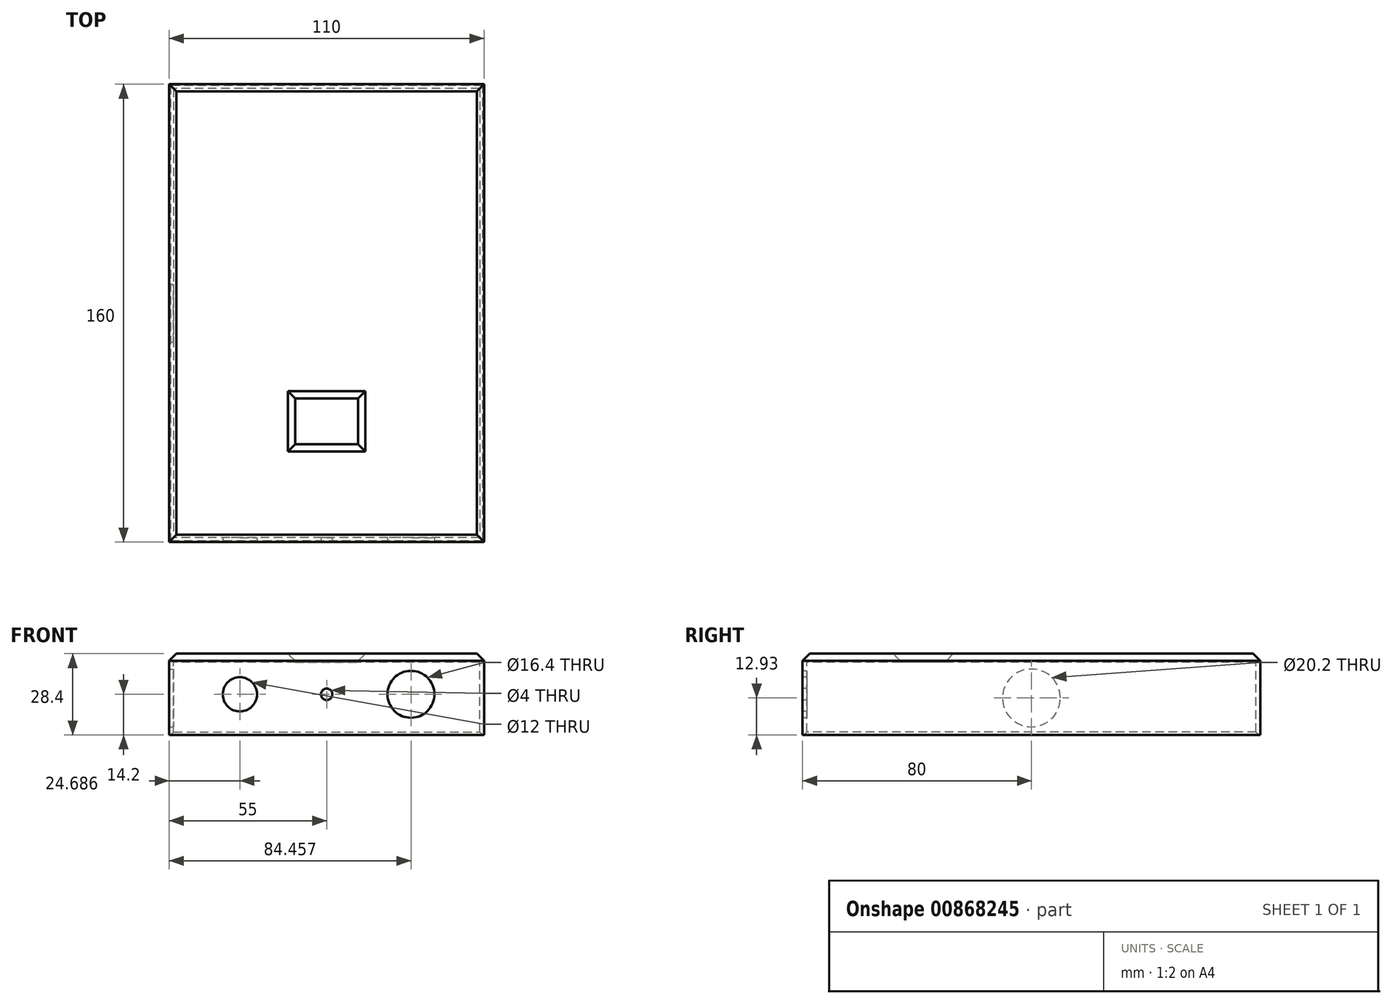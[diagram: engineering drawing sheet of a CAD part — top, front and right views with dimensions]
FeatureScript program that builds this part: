
annotation { "Feature Type Name" : "Feature", "Feature Type Description" : "" }
export const myFeature = defineFeature(function(context is Context, id is Id, definition is map)
    precondition{}
    {
        {
            var Q0;
            Q0=qCreatedBy(makeId("Top.planeOp"),FACE);
            var sketch = newSketch(context, id + "F0", { "sketchPlane" : qUnion([Q0])});
            skLineSegment(sketch, "E0.bottom", {"start": v(-55, -80) * mm, "end": v(55, -80) * mm});
            skLineSegment(sketch, "E0.top", {"start": v(-55, 80) * mm, "end": v(55, 80) * mm});
            skLineSegment(sketch, "E0.left", {"start": v(-55, -80) * mm, "end": v(-55, 80) * mm});
            skLineSegment(sketch, "E0.right", {"start": v(55, -80) * mm, "end": v(55, 80) * mm});
            skPoint(sketch, "E0.middle", {"position": v(0, 0) * mm});
            skLineSegment(sketch, "E1.bottom", {"start": v(-11, -29.82) * mm, "end": v(11, -29.82) * mm});
            skLineSegment(sketch, "E1.top", {"start": v(-11, -45.82) * mm, "end": v(11, -45.82) * mm});
            skLineSegment(sketch, "E1.left", {"start": v(-11, -29.82) * mm, "end": v(-11, -45.82) * mm});
            skLineSegment(sketch, "E1.right", {"start": v(11, -29.82) * mm, "end": v(11, -45.82) * mm});
            skPoint(sketch, "E1.middle", {"position": v(0, -37.82) * mm});
            skSolve(sketch);
        }
        {
            var Q0;
            Q0=makeQuery(id+"F0.imprint","IMPRINT",FACE,{"disambiguationData":[TD([[makeQuery(id+"F0.imprint","IMPRINT",EDGE,{"derivedFrom":sQuery(id+"F0.wireOp",EDGE,"E0.bottom")}),1.0]])]});
            extrude(context, id + "F1", {"entities" : qUnion([Q0]), "depth" : 3 * mm, "offsetDistance" : 25.4 * mm});
        }
        {
            var Q0;
            Q0=makeQuery(id+"F1.opExtrude","CAP_FACE",FACE,{"disambiguationData":[OSD([sQuery(id+"F0.wireOp",EDGE,"E0.bottom"),sQuery(id+"F0.wireOp",EDGE,"E0.top"),sQuery(id+"F0.wireOp",EDGE,"E0.left"),sQuery(id+"F0.wireOp",EDGE,"E0.right")])],"isStart":true});
            var sketch = newSketch(context, id + "F2", { "sketchPlane" : qUnion([Q0])});
            skLineSegment(sketch, "E2.bottom", {"start": v(53.5, -78.5) * mm, "end": v(-53.5, -78.5) * mm});
            skLineSegment(sketch, "E2.top", {"start": v(53.5, 78.5) * mm, "end": v(-53.5, 78.5) * mm});
            skLineSegment(sketch, "E2.left", {"start": v(53.5, -78.5) * mm, "end": v(53.5, 78.5) * mm});
            skLineSegment(sketch, "E2.right", {"start": v(-53.5, -78.5) * mm, "end": v(-53.5, 78.5) * mm});
            skPoint(sketch, "E2.middle", {"position": v(0, 0) * mm});
            skSolve(sketch);
        }
        {
            var Q0;
            Q0=makeQuery(id+"F2.imprint","IMPRINT",FACE,{"disambiguationData":[TD([[makeQuery(id+"F2.imprint","IMPRINT",EDGE,{"derivedFrom":sQuery(id+"F2.wireOp",EDGE,"E2.bottom")}),1.0]])]});
            extrude(context, id + "F3", {"entities" : qUnion([Q0]), "operationType" : NewBodyOperationType.ADD, "depth" : 25.4 * mm, "offsetDistance" : 25.4 * mm});
        }
        {
            var Q0;
            {var subQ0=sQuery(id+"F0.wireOp",EDGE,"E0.bottom");Q0=makeQuery(id+"F3.boolean.opBoolean","MERGE",FACE,{"derivedFrom":[makeQuery(id+"F1.opExtrude","SWEPT_FACE",FACE,{"disambiguationData":[OSD([subQ0])]}),makeQuery(id+"F3.opExtrude","SWEPT_FACE",FACE,{"disambiguationData":[OSD([subQ0])]})]});}
            var sketch = newSketch(context, id + "F4", { "sketchPlane" : qUnion([Q0])});
            skCircle(sketch, "E3", {"center": v(0, -11.2) * mm, "radius": 2 * mm});
            skPoint(sketch, "E3.centerSnap0", {"position": v(55, -11.2) * mm});
            skCircle(sketch, "E4", {"center": v(29.46, -11.2) * mm, "radius": 8.2 * mm});
            skCircle(sketch, "E5", {"center": v(-30.31, -11.2) * mm, "radius": 6 * mm});
            skPoint(sketch, "E5.centerSnap0", {"position": v(-55, -11.2) * mm});
            skSolve(sketch);
        }
        {
            var Q0;
            Q0=sQuery(id+"F4.wireOp",VERTEX,"E4.center");
            var Q1;
            Q1=makeQuery(id+"F1.opExtrude","SWEPT_BODY",BODY,{"disambiguationData":[OSD([sQuery(id+"F0.wireOp",EDGE,"E0.bottom"),sQuery(id+"F0.wireOp",EDGE,"E0.top"),sQuery(id+"F0.wireOp",EDGE,"E0.left"),sQuery(id+"F0.wireOp",EDGE,"E0.right")])]});
            hole(context, id + "F5", {"style" : HoleStyle.SIMPLE, "endStyle" : HoleEndStyle.BLIND, "holeDiameter" : 16.4 * mm, "majorDiameter" : 6.35 * mm, "holeDepth" : 7.62 * mm, "isTappedThrough" : true, "tappedDepth" : 12.7 * mm, "tapClearance" : 3, "locations" : qUnion([Q0]), "scope" : qUnion([Q1])});
        }
        {
            var Q0;
            Q0=sQuery(id+"F4.wireOp",VERTEX,"E3.center");
            var Q1;
            Q1=makeQuery(id+"F1.opExtrude","SWEPT_BODY",BODY,{"disambiguationData":[OSD([sQuery(id+"F0.wireOp",EDGE,"E0.bottom"),sQuery(id+"F0.wireOp",EDGE,"E0.top"),sQuery(id+"F0.wireOp",EDGE,"E0.left"),sQuery(id+"F0.wireOp",EDGE,"E0.right")])]});
            hole(context, id + "F6", {"style" : HoleStyle.SIMPLE, "endStyle" : HoleEndStyle.BLIND, "holeDiameter" : 4 * mm, "majorDiameter" : 6.35 * mm, "holeDepth" : 7.62 * mm, "isTappedThrough" : true, "tappedDepth" : 12.7 * mm, "tapClearance" : 3, "locations" : qUnion([Q0]), "scope" : qUnion([Q1])});
        }
        {
            var Q0;
            Q0=sQuery(id+"F4.wireOp",VERTEX,"E5.center");
            var Q1;
            Q1=makeQuery(id+"F1.opExtrude","SWEPT_BODY",BODY,{"disambiguationData":[OSD([sQuery(id+"F0.wireOp",EDGE,"E0.bottom"),sQuery(id+"F0.wireOp",EDGE,"E0.top"),sQuery(id+"F0.wireOp",EDGE,"E0.left"),sQuery(id+"F0.wireOp",EDGE,"E0.right")])]});
            hole(context, id + "F7", {"style" : HoleStyle.SIMPLE, "endStyle" : HoleEndStyle.BLIND, "holeDiameter" : 12 * mm, "majorDiameter" : 6.35 * mm, "holeDepth" : 7.62 * mm, "isTappedThrough" : true, "tappedDepth" : 12.7 * mm, "tapClearance" : 3, "locations" : qUnion([Q0]), "scope" : qUnion([Q1])});
        }
        {
            var Q0;
            Q0=makeQuery(id+"F3.opExtrude","CAP_EDGE",EDGE,{"disambiguationData":[OSD([sQuery(id+"F2.wireOp",EDGE,"E2.left")])],"isStart":false});
            var Q1;
            Q1=makeQuery(id+"F3.opExtrude","CAP_EDGE",EDGE,{"disambiguationData":[OSD([sQuery(id+"F2.wireOp",EDGE,"E2.bottom")])],"isStart":false});
            var Q2;
            Q2=makeQuery(id+"F3.opExtrude","CAP_EDGE",EDGE,{"disambiguationData":[OSD([sQuery(id+"F2.wireOp",EDGE,"E2.right")])],"isStart":false});
            var Q3;
            Q3=makeQuery(id+"F3.opExtrude","CAP_EDGE",EDGE,{"disambiguationData":[OSD([sQuery(id+"F2.wireOp",EDGE,"E2.top")])],"isStart":false});
            chamfer(context, id + "F8", {"entities" : qUnion([Q0, Q1, Q2, Q3]), "width" : 1 * mm, "tangentPropagation" : true});
        }
        {
            var Q0;
            Q0=makeQuery(id+"F1.opExtrude","CAP_EDGE",EDGE,{"disambiguationData":[OSD([sQuery(id+"F0.wireOp",EDGE,"E1.top")])],"isStart":false});
            var Q1;
            Q1=makeQuery(id+"F1.opExtrude","CAP_EDGE",EDGE,{"disambiguationData":[OSD([sQuery(id+"F0.wireOp",EDGE,"E1.left")])],"isStart":false});
            var Q2;
            Q2=makeQuery(id+"F1.opExtrude","CAP_EDGE",EDGE,{"disambiguationData":[OSD([sQuery(id+"F0.wireOp",EDGE,"E1.right")])],"isStart":false});
            var Q3;
            Q3=makeQuery(id+"F1.opExtrude","CAP_FACE",FACE,{"disambiguationData":[OSD([sQuery(id+"F0.wireOp",EDGE,"E0.bottom"),sQuery(id+"F0.wireOp",EDGE,"E0.top"),sQuery(id+"F0.wireOp",EDGE,"E0.left"),sQuery(id+"F0.wireOp",EDGE,"E0.right"),sQuery(id+"F0.wireOp",EDGE,"E1.bottom"),sQuery(id+"F0.wireOp",EDGE,"E1.top"),sQuery(id+"F0.wireOp",EDGE,"E1.left"),sQuery(id+"F0.wireOp",EDGE,"E1.right")])],"isStart":false});
            chamfer(context, id + "F9", {"entities" : qUnion([Q0, Q1, Q2, Q3]), "width" : 2.54 * mm, "tangentPropagation" : true});
        }
        {
            var Q0;
            {var subQ0=sQuery(id+"F0.wireOp",EDGE,"E0.left");Q0=makeQuery(id+"F3.boolean.opBoolean","MERGE",FACE,{"derivedFrom":[makeQuery(id+"F1.opExtrude","SWEPT_FACE",FACE,{"disambiguationData":[OSD([subQ0])]}),makeQuery(id+"F3.opExtrude","SWEPT_FACE",FACE,{"disambiguationData":[OSD([subQ0])]})]});}
            var sketch = newSketch(context, id + "F10", { "sketchPlane" : qUnion([Q0])});
            skCircle(sketch, "E6", {"center": v(0, -12.47) * mm, "radius": 10.1 * mm});
            skPoint(sketch, "E6.centerSnap0", {"position": v(-80, -12.47) * mm});
            skSolve(sketch);
        }
        {
            var Q0;
            Q0=makeQuery(id+"F10.imprint","IMPRINT",FACE,{"disambiguationData":[TD([[makeQuery(id+"F10.imprint","IMPRINT",EDGE,{"derivedFrom":sQuery(id+"F10.wireOp",EDGE,"E6")}),1.0]])]});
            extrude(context, id + "F11", {"entities" : qUnion([Q0]), "operationType" : NewBodyOperationType.REMOVE, "endBound" : BoundingType.SYMMETRIC, "depth" : 25.4 * mm, "offsetDistance" : 25.4 * mm});
        }
    });
